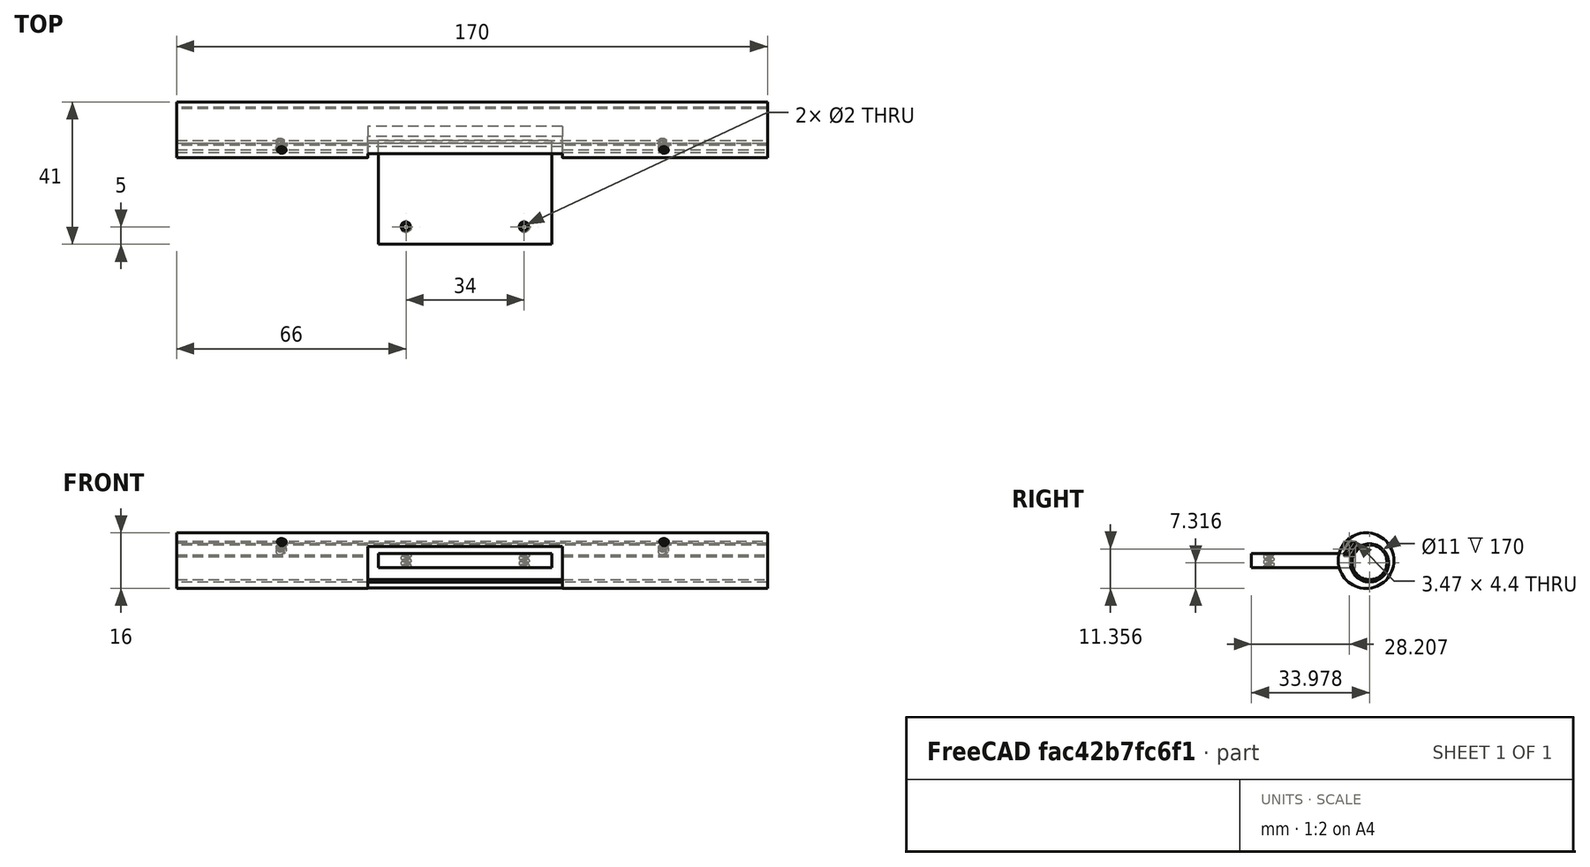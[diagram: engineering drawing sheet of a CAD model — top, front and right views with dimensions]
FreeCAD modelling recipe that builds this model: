
FCSTD DOCUMENT  (FreeCAD 0.21R33694 (Git))
Label: brazo
License: Creative Commons Attribution-ShareAlike
LicenseURL: http://creativecommons.org/licenses/by-sa/4.0/
objects: Part::Feature×4, Part::Cut×4, Part::Box×2, Part::MultiFuse×1, Sketcher::SketchObject×1, PartDesign::Pad×1, PartDesign::Body×1, Part::Cylinder×1
note: 16 computed .brp shape members not serialized (recipe doc carries the construction recipe); baked Part::Feature solids carry a one-line shape summary decoded from their .brp

FEATURE [Part::Box] Box  label="Cubo"
  AttacherType = Attacher::AttachEngine3D
  Height = 4
  Length = 50
  Placement = pos=(-25,22,-7.5) rot=(0,0,1;0rad)
  Width = 30
FEATURE [Part::Feature] Fusion001005  label="Rosca macho006"
  Placement = pos=(-17,27,-10) rot=(0,0,1;0rad)
  shape: bbox 3.919 x 4.387 x 44 mm, 35 faces (baked)
FEATURE [Part::Feature] Fusion001006  label="Rosca macho007"
  Placement = pos=(17,27,-10) rot=(0,0,1;0rad)
  shape: bbox 3.919 x 4.387 x 44 mm, 35 faces (baked)
FEATURE [Part::MultiFuse] Fusion001007
  Refine = true
  Shapes = -> [Fusion001005,Fusion001006]
FEATURE [Part::Cut] Cut001  label="Soporte_eje"
  Base = -> Box
  Placement = pos=(-117,36,0) rot=(0,0,1;0rad)
  Refine = true
  Tool = -> Fusion001007
FEATURE [Sketcher::SketchObject] Sketch007
  FullyConstrained = false
  MapMode = 5
  Placement = pos=(0,0,0) rot=(0.57735,0.57735,0.57735;2.0944rad)
  Support = -> [YZ_Plane003]
  sketch-geometry (6):
    g0: Circle CenterX=0 CenterY=0 CenterZ=0 NormalX=0 NormalY=0 NormalZ=1 AngleXU=0 Radius=8
    g1: Circle CenterX=0 CenterY=-1.19343 CenterZ=0 NormalX=0 NormalY=0 NormalZ=1 AngleXU=0 Radius=5.5
    g2: LineSegment StartX=-2.35964 StartY=6.31767 StartZ=0 EndX=2.35964 EndY=6.31767 EndZ=0
    g3: LineSegment StartX=2.35964 StartY=6.31767 StartZ=0 EndX=2.35964 EndY=5.38418 EndZ=0
    g4: LineSegment StartX=2.35964 StartY=5.38418 StartZ=0 EndX=-2.35964 EndY=5.38418 EndZ=0
    g5: LineSegment StartX=-2.35964 StartY=5.38418 StartZ=0 EndX=-2.35964 EndY=6.31767 EndZ=0
  constraints (12):
    c: Coincident(g0,g-1)
    c: Coincident(g2,g3)
    c: Coincident(g3,g4)
    c: Coincident(g4,g5)
    c: Coincident(g5,g2)
    c: Horizontal(g4)
    c: Vertical(g3)
    c: Vertical(g5)
    c: Symmetric(g2,g2,g-2)
    c: PointOnObject(g1,g-2)
    c: Radius(g0) = 8
    c: Radius(g1) = 5.5
FEATURE [PartDesign::Pad] Pad003
  Direction = (1,-2e-16,3e-16)
  Length = 170
  Length2 = 100
  Placement = pos=(0,0,0) rot=(0.57735,0.57735,0.57735;2.0944rad)
  Profile = -> Sketch007
  Refine = true
  Type = 0
FEATURE [PartDesign::Body] Body003
  Group = -> [Sketch007,Pad003]
  Origin = -> Origin003
  Placement = pos=(-200,91,-5.5) rot=(1,0,0;0.959931rad)
  Tip = -> Pad003
FEATURE [Part::Cylinder] Cylinder  label="Cilindro-movil"
  Angle = 360
  AttacherType = Attacher::AttachEngine3D
  FirstAngle = 0
  Height = 170
  Placement = pos=(-200,92,-6) rot=(0,1,0;1.5708rad)
  Radius = 5
  SecondAngle = 0
FEATURE [Part::Box] Box001  label="Cubo001"
  AttacherType = Attacher::AttachEngine3D
  Height = 20
  Length = 56
  Placement = pos=(-145,76,-21.5) rot=(0,0,1;0rad)
  Width = 16
FEATURE [Part::Cut] Cut
  Base = -> Body003
  Refine = true
  Tool = -> Box001
FEATURE [Part::Feature] Fusion001008  label="Rosca macho008"
  Placement = pos=(-170,93.75,-8.78) rot=(0.819304,0.219813,-0.52955;0.936369rad)
  shape: bbox 4.221 x 33 x 32.52 mm, 35 faces (baked)
FEATURE [Part::Cut] Cut023
  Base = -> Cut
  Refine = true
  Tool = -> Fusion001008
FEATURE [Part::Feature] Fusion001009  label="Rosca macho009"
  Placement = pos=(-60,93.75,-8.78) rot=(0.82,0.22,-0.53;0.936369rad)
  shape: bbox 4.221 x 33 x 32.52 mm, 35 faces (baked)
FEATURE [Part::Cut] Cut024  label="cilindro-fijo"
  Base = -> Cut023
  Refine = true
  Tool = -> Fusion001009
